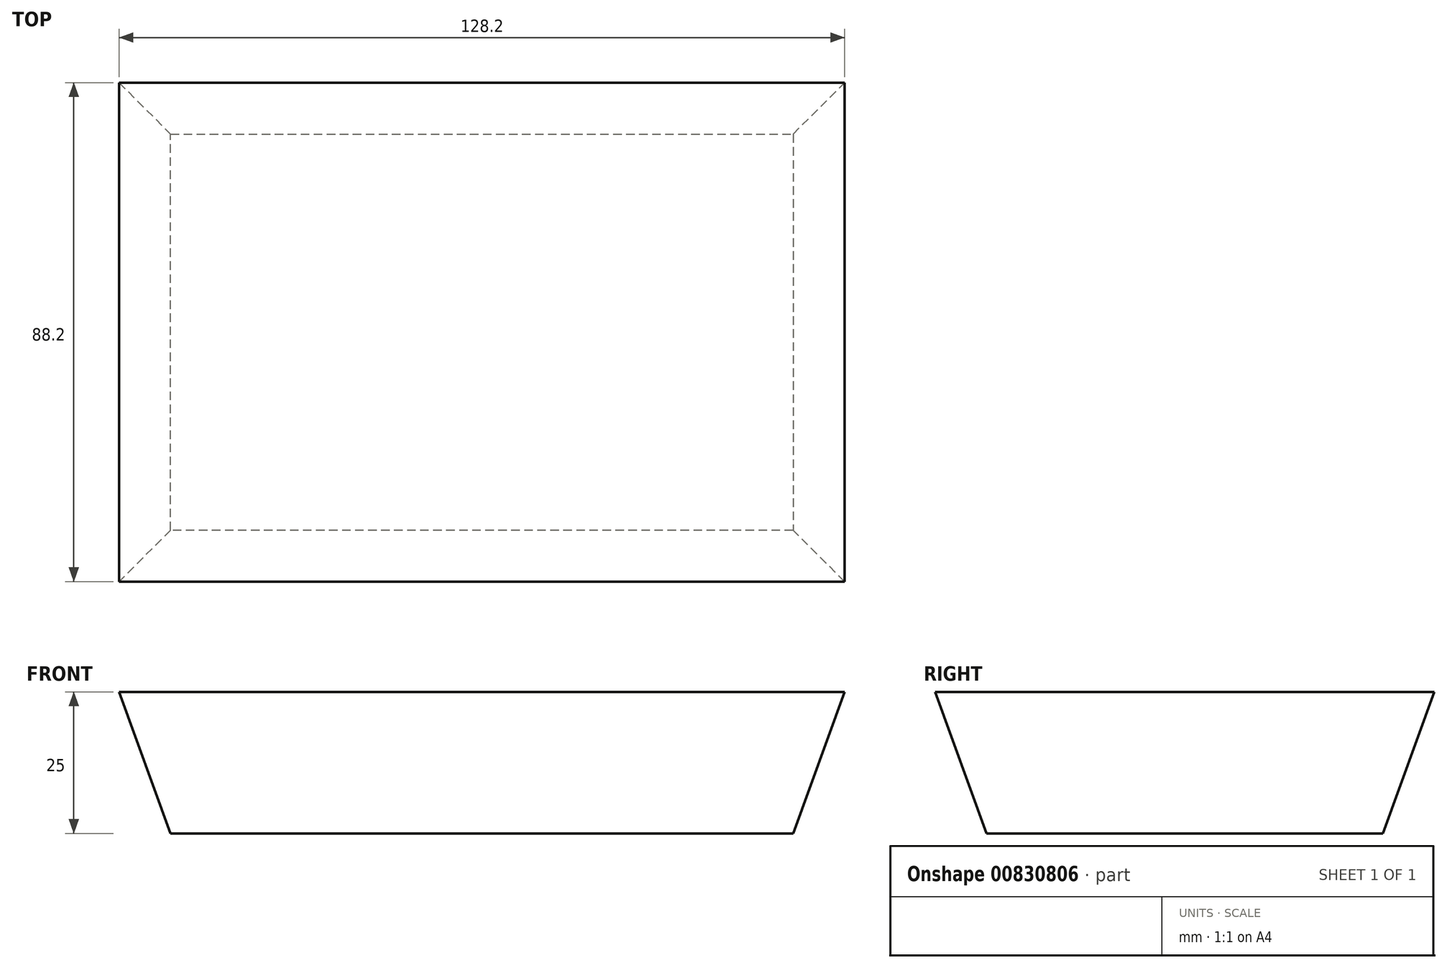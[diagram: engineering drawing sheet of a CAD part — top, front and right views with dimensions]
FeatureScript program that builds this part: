
annotation { "Feature Type Name" : "Feature", "Feature Type Description" : "" }
export const myFeature = defineFeature(function(context is Context, id is Id, definition is map)
    precondition{}
    {
        {
            var Q0;
            Q0=qCreatedBy(makeId("Top.planeOp"),FACE);
            var sketch = newSketch(context, id + "F0", { "sketchPlane" : qUnion([Q0])});
            skLineSegment(sketch, "E0.bottom", {"start": v(55, 35) * mm, "end": v(-55, 35) * mm});
            skLineSegment(sketch, "E0.top", {"start": v(55, -35) * mm, "end": v(-55, -35) * mm});
            skLineSegment(sketch, "E0.left", {"start": v(55, 35) * mm, "end": v(55, -35) * mm});
            skLineSegment(sketch, "E0.right", {"start": v(-55, 35) * mm, "end": v(-55, -35) * mm});
            skPoint(sketch, "E0.middle", {"position": v(0, 0) * mm});
            skSolve(sketch);
        }
        {
            var Q0;
            Q0=makeQuery(id+"F0.imprint","IMPRINT",FACE,{"disambiguationData":[TD([[makeQuery(id+"F0.imprint","IMPRINT",EDGE,{"derivedFrom":sQuery(id+"F0.wireOp",EDGE,"E0.bottom")}),1.0]])]});
            extrude(context, id + "F1", {"entities" : qUnion([Q0]), "depth" : 25 * mm, "offsetDistance" : 25 * mm, "hasDraft" : true, "draftAngle" : 20 * degree});
        }
    });
